# Revit family: Atlas Basin 55cm 1th
name_source: partatom
category: Plumbing Fixtures
units: mm (PartAtom-declared; Revit-internal decimal feet)

## family parameters
Always vertical = Yes
Cut with Voids When Loaded = No
Enable Cutting in Views = No
Maintain Annotation Orientation = No
OmniClass Number = 23.45.05.14.99
OmniClass Title = Other Sanitary Washing Plumbing Fixtures
Part Type = Normal
Room Calculation Point = No
Round Connector Dimension = Use Diameter
Shared = No
Work Plane-Based = No

## types (3) — shared parameters
Category = Basins – Wall Hung
Colour = White
Fixing Details = Basin Fixing Bolts not supplied, 8mm to 10mm bolts recommended
Manufacturer = Lecico SA
Material = Vitreous China
URL = https://www.lecicosa.co.za
zero-valued in all types: Default Elevation

## per-type parameters (varying)
| type | Half Pedestal | Model | No Pedestal | Product Code | Technical Dimensions | With Full Pedestal |
| Atlas Basin 55cm 1th with Full Pedestal | No | Atlas Basin 55cm 1th with Full Pedestal | No | ATLBASWHU1550UE, GEOPEDFUL0000UE | W558 x H820 x D463mm | Yes |
| Atlas Basin 55cm 1th - no pedestal | No | Atlas Basin 55cm 1th - no pedestal | Yes | ATLBASWHU1550UE | W558 x H185 x D463mm | No |
| Atlas Basin 55cm 1th with Half Pedestal | Yes | Atlas Basin 55cm 1th - with half pedestal | Yes | ATLBASWHU1550UE, MADPEDSEM0000UE | W558 x H185 x D463mm | No |

## geometry (parser evidence)
native form markers: Sweep x9
no freeform markers — native parametric forms only
